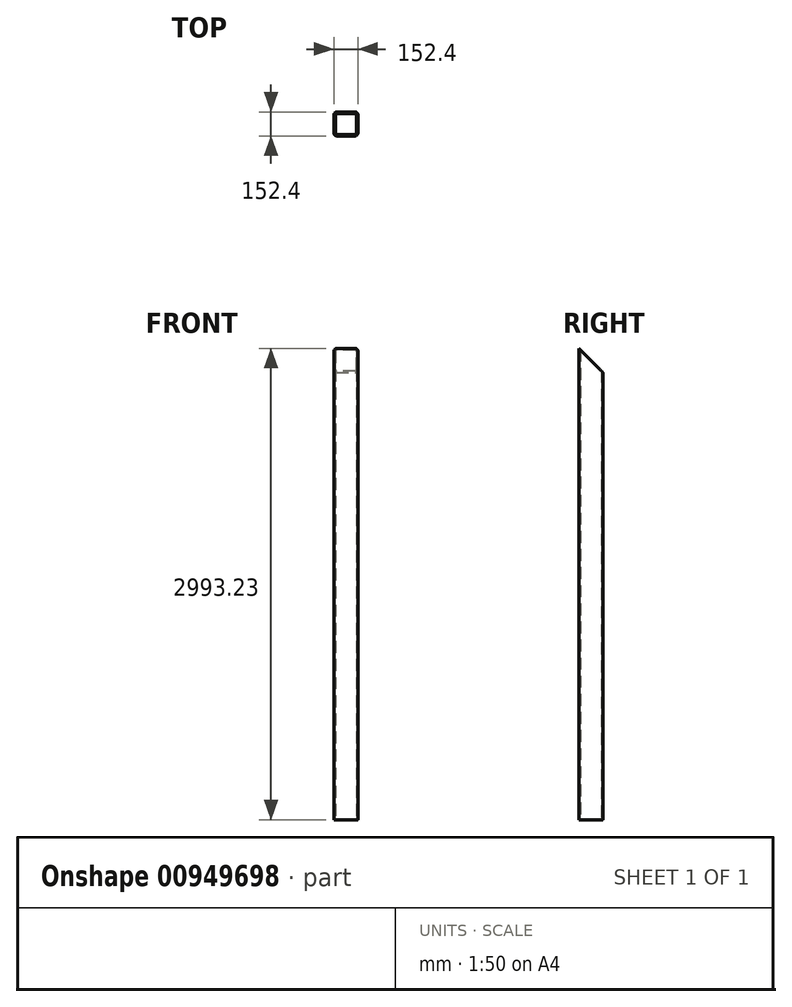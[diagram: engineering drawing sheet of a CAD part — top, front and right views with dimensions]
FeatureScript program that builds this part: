
annotation { "Feature Type Name" : "Feature", "Feature Type Description" : "" }
export const myFeature = defineFeature(function(context is Context, id is Id, definition is map)
    precondition{}
    {
        {
            var Q0;
            Q0=qCreatedBy(makeId("Top.planeOp"),FACE);
            var sketch = newSketch(context, id + "F0", { "sketchPlane" : qUnion([Q0])});
            skLineSegment(sketch, "E0.bottom", {"start": v(-57.15, -76.2) * mm, "end": v(57.15, -76.2) * mm});
            skLineSegment(sketch, "E0.top", {"start": v(-57.15, 76.2) * mm, "end": v(57.15, 76.2) * mm});
            skLineSegment(sketch, "E0.left", {"start": v(-76.2, -57.15) * mm, "end": v(-76.2, 57.15) * mm});
            skLineSegment(sketch, "E0.right", {"start": v(76.2, -57.15) * mm, "end": v(76.2, 57.15) * mm});
            skPoint(sketch, "E0.middle", {"position": v(0, 0) * mm});
            skLineSegment(sketch, "E1.bottom", {"start": v(-57.15, -66.68) * mm, "end": v(57.15, -66.68) * mm});
            skLineSegment(sketch, "E1.top", {"start": v(-57.15, 66.68) * mm, "end": v(57.15, 66.68) * mm});
            skLineSegment(sketch, "E1.left", {"start": v(-66.68, -57.15) * mm, "end": v(-66.68, 57.15) * mm});
            skLineSegment(sketch, "E1.right", {"start": v(66.68, -57.15) * mm, "end": v(66.68, 57.15) * mm});
            skPoint(sketch, "E2.visualSharp", {"position": v(-76.2, 76.2) * mm});
            skArc(sketch, "E2.filletArc", {"start": v(-57.15, 76.2) * mm, "mid": v(-70.62, 70.62) * mm, "end": v(-76.2, 57.15) * mm});
            skPoint(sketch, "E3.visualSharp", {"position": v(-76.2, -76.2) * mm});
            skArc(sketch, "E3.filletArc", {"start": v(-76.2, -57.15) * mm, "mid": v(-70.62, -70.62) * mm, "end": v(-57.15, -76.2) * mm});
            skPoint(sketch, "E4.visualSharp", {"position": v(76.2, -76.2) * mm});
            skArc(sketch, "E4.filletArc", {"start": v(57.15, -76.2) * mm, "mid": v(70.62, -70.62) * mm, "end": v(76.2, -57.15) * mm});
            skPoint(sketch, "E5.visualSharp", {"position": v(76.2, 76.2) * mm});
            skArc(sketch, "E5.filletArc", {"start": v(76.2, 57.15) * mm, "mid": v(70.62, 70.62) * mm, "end": v(57.15, 76.2) * mm});
            skPoint(sketch, "E6.visualSharp", {"position": v(-66.68, 66.68) * mm});
            skArc(sketch, "E6.filletArc", {"start": v(-57.15, 66.68) * mm, "mid": v(-63.89, 63.89) * mm, "end": v(-66.68, 57.15) * mm});
            skPoint(sketch, "E7.visualSharp", {"position": v(-66.68, -66.68) * mm});
            skArc(sketch, "E7.filletArc", {"start": v(-66.68, -57.15) * mm, "mid": v(-63.89, -63.89) * mm, "end": v(-57.15, -66.68) * mm});
            skPoint(sketch, "E8.visualSharp", {"position": v(66.68, -66.68) * mm});
            skArc(sketch, "E8.filletArc", {"start": v(57.15, -66.68) * mm, "mid": v(63.89, -63.89) * mm, "end": v(66.68, -57.15) * mm});
            skPoint(sketch, "E9.visualSharp", {"position": v(66.68, 66.68) * mm});
            skArc(sketch, "E9.filletArc", {"start": v(66.68, 57.15) * mm, "mid": v(63.89, 63.89) * mm, "end": v(57.15, 66.68) * mm});
            skSolve(sketch);
        }
        {
            var Q0;
            Q0=qSketchRegion(id+"F0",true);
            extrude(context, id + "F1", {"entities" : qUnion([Q0]), "depth" : 2993.23 * mm, "offsetDistance" : 25.4 * mm});
        }
        {
            var Q0;
            Q0=qCreatedBy(makeId("Right.planeOp"),FACE);
            var sketch = newSketch(context, id + "F2", { "sketchPlane" : qUnion([Q0])});
            skLineSegment(sketch, "E10", {"start": v(-76.2, 2993.23) * mm, "end": v(76.2, 2993.23) * mm});
            skLineSegment(sketch, "E11", {"start": v(-76.2, 2993.23) * mm, "end": v(76.2, 2840.83) * mm});
            skLineSegment(sketch, "E12", {"start": v(76.2, 2993.23) * mm, "end": v(76.2, 2840.83) * mm});
            skSolve(sketch);
        }
        {
            var Q0;
            Q0 = qSketchRegion(id + "F2", true);
            extrude(context, id + "F3", {"entities" : qUnion([Q0]), "operationType" : NewBodyOperationType.REMOVE, "endBound" : BoundingType.THROUGH_ALL, "oppositeDirection" : true, "depth" : 25.4 * mm, "offsetDistance" : 25.4 * mm, "hasSecondDirection" : true, "secondDirectionBound" : SecondDirectionBoundingType.THROUGH_ALL, "secondDirectionOppositeDirection" : false, "secondDirectionDepth" : 25.4 * mm});
        }
    });
